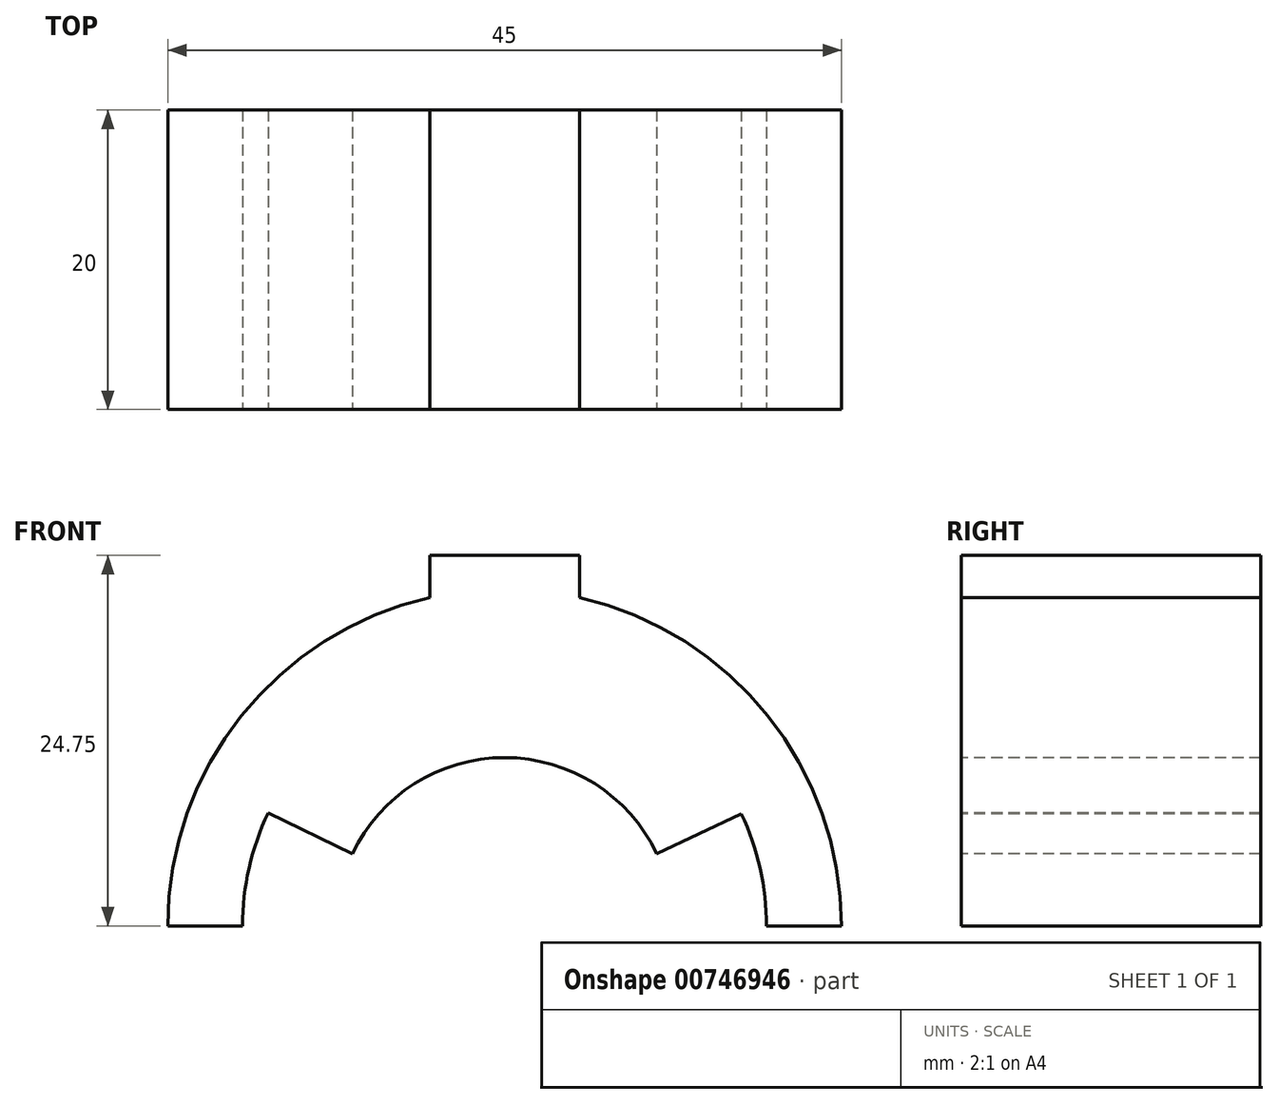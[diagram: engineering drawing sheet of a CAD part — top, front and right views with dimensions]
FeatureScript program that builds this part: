
annotation { "Feature Type Name" : "Feature", "Feature Type Description" : "" }
export const myFeature = defineFeature(function(context is Context, id is Id, definition is map)
    precondition{}
    {
        {
            var Q0;
            Q0=qCreatedBy(makeId("Front.planeOp"),FACE);
            var sketch = newSketch(context, id + "F0", { "sketchPlane" : qUnion([Q0])});
            skLineSegment(sketch, "E0", {"start": v(24.92, 23.9) * mm, "end": v(19.3, 26.63) * mm});
            skLineSegment(sketch, "E1", {"start": v(45.25, 23.9) * mm, "end": v(50.9, 26.58) * mm});
            skArc(sketch, "E2", {"start": v(50.9, 26.58) * mm, "mid": v(35.12, 36.58) * mm, "end": v(19.3, 26.63) * mm});
            skArc(sketch, "E3", {"start": v(24.92, 23.9) * mm, "mid": v(35.09, 30.33) * mm, "end": v(45.25, 23.9) * mm});
            skLineSegment(sketch, "E4", {"start": v(35.09, 30.33) * mm, "end": v(40.09, 30.33) * mm});
            skLineSegment(sketch, "E5", {"start": v(40.09, 30.33) * mm, "end": v(30.09, 30.33) * mm});
            skLineSegment(sketch, "E6.bottom", {"start": v(30.09, 30.33) * mm, "end": v(40.09, 30.33) * mm});
            skLineSegment(sketch, "E6.top", {"start": v(30.09, 43.83) * mm, "end": v(40.09, 43.83) * mm});
            skLineSegment(sketch, "E6.left", {"start": v(30.09, 30.33) * mm, "end": v(30.09, 43.83) * mm});
            skLineSegment(sketch, "E6.right", {"start": v(40.09, 30.33) * mm, "end": v(40.09, 43.83) * mm});
            skArc(sketch, "E7", {"start": v(21.68, 30.33) * mm, "mid": v(18.64, 25.06) * mm, "end": v(17.59, 19.08) * mm});
            skArc(sketch, "E8", {"start": v(48.5, 30.33) * mm, "mid": v(51.53, 25.06) * mm, "end": v(52.59, 19.08) * mm});
            skLineSegment(sketch, "E9", {"start": v(12.59, 19.08) * mm, "end": v(17.59, 19.08) * mm});
            skLineSegment(sketch, "E10", {"start": v(52.59, 19.08) * mm, "end": v(57.59, 19.08) * mm});
            skArc(sketch, "E11", {"start": v(12.59, 19.08) * mm, "mid": v(35.09, 41.58) * mm, "end": v(57.59, 19.08) * mm});
            skLineSegment(sketch, "E12", {"start": v(35.09, 19.08) * mm, "end": v(35.09, 30.33) * mm});
            skSolve(sketch);
        }
        {
            var Q0;
            {var subQ2=sQuery(id+"F0.wireOp",EDGE,"E9");Q0=makeQuery(id+"F0.imprint","IMPRINT",FACE,{"disambiguationData":[TD([[makeQuery(id+"F0.imprint","IMPRINT",EDGE,{"derivedFrom":subQ2}),1.0]])]});}
            var Q1;
            {var subQ0=sQuery(id+"F0.wireOp",EDGE,"E6.top");Q1=makeQuery(id+"F0.imprint","IMPRINT",FACE,{"disambiguationData":[TD([[makeQuery(id+"F0.imprint","IMPRINT",EDGE,{"derivedFrom":subQ0}),-1.0]])]});}
            var Q2;
            {var subQ0=sQuery(id+"F0.wireOp",EDGE,"E6.right");var subQ1=sQuery(id+"F0.wireOp",EDGE,"E2");var subQ2=makeQuery(id+"F0.imprint","INTERSECT",VERTEX,{"derivedFrom":[subQ1,subQ0]});Q2=makeQuery(id+"F0.imprint","IMPRINT",FACE,{"disambiguationData":[TD([[makeQuery(id+"F0.imprint","IMPRINT",EDGE,{"disambiguationData":[TD([[subQ2,-1.0]])],"derivedFrom":subQ1}),-1.0]])]});}
            var Q3;
            {var subQ4=sQuery(id+"F0.wireOp",EDGE,"E10");Q3=makeQuery(id+"F0.imprint","IMPRINT",FACE,{"disambiguationData":[TD([[makeQuery(id+"F0.imprint","IMPRINT",EDGE,{"derivedFrom":subQ4}),1.0]])]});}
            var Q4;
            {var subQ9=sQuery(id+"F0.wireOp",EDGE,"E0");Q4=makeQuery(id+"F0.imprint","IMPRINT",FACE,{"disambiguationData":[TD([[makeQuery(id+"F0.imprint","IMPRINT",EDGE,{"derivedFrom":subQ9}),-1.0]])]});}
            var Q5;
            {var subQ3=sQuery(id+"F0.wireOp",EDGE,"E2");var subQ6=sQuery(id+"F0.wireOp",EDGE,"E6.right");var subQ8=makeQuery(id+"F0.imprint","INTERSECT",VERTEX,{"derivedFrom":[subQ3,subQ6]});Q5=makeQuery(id+"F0.imprint","IMPRINT",FACE,{"disambiguationData":[TD([[makeQuery(id+"F0.imprint","IMPRINT",EDGE,{"disambiguationData":[TD([[subQ8,-1.0]])],"derivedFrom":subQ3}),1.0]])]});}
            var Q6;
            {var subQ9=sQuery(id+"F0.wireOp",EDGE,"E1");Q6=makeQuery(id+"F0.imprint","IMPRINT",FACE,{"disambiguationData":[TD([[makeQuery(id+"F0.imprint","IMPRINT",EDGE,{"derivedFrom":subQ9}),1.0]])]});}
            extrude(context, id + "F1", {"entities" : qUnion([Q0, Q1, Q2, Q3, Q4, Q5, Q6]), "oppositeDirection" : true, "depth" : 20 * mm, "offsetDistance" : 25 * mm});
        }
    });
